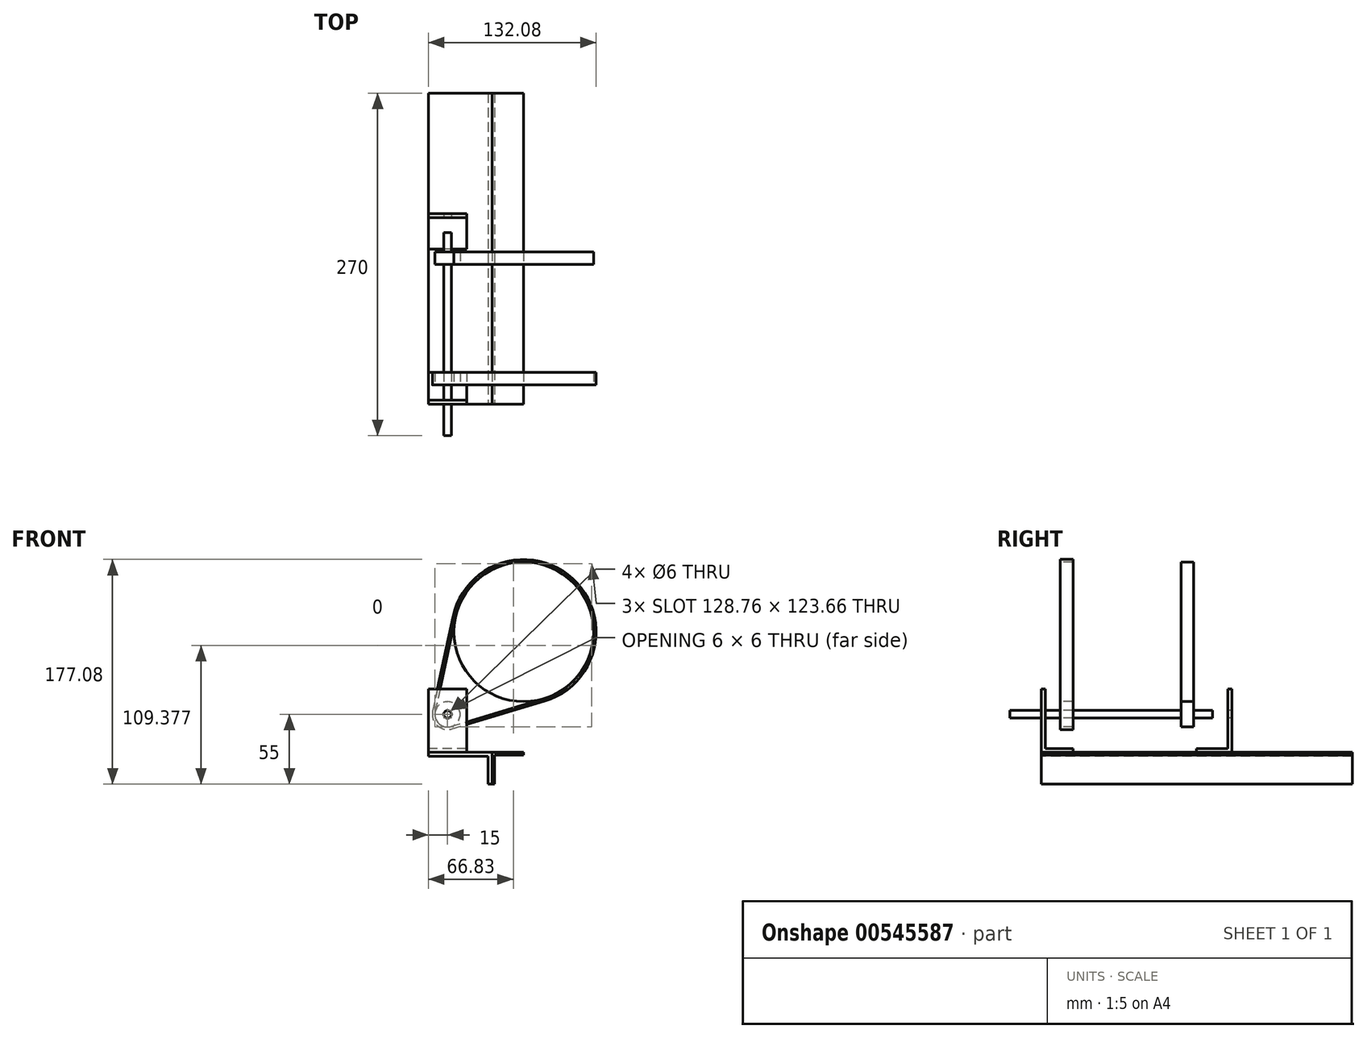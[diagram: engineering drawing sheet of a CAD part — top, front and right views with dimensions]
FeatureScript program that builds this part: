
annotation { "Feature Type Name" : "Feature", "Feature Type Description" : "" }
export const myFeature = defineFeature(function(context is Context, id is Id, definition is map)
    precondition{}
    {
        {
            var Q0;
            Q0=qCreatedBy(makeId("Front.planeOp"),FACE);
            cPlane(context, id + "F0", {"entities" : qUnion([Q0]), "cplaneType" : CPlaneType.OFFSET, "offset" : 15 * mm, "oppositeDirection" : true, "width" : 150 * mm, "height" : 150 * mm});
        }
        {
            var Q0;
            Q0=qCreatedBy(id+"F0.planeOp",FACE);
            cPlane(context, id + "F1", {"entities" : qUnion([Q0]), "cplaneType" : CPlaneType.OFFSET, "offset" : 95 * mm, "oppositeDirection" : true, "width" : 150 * mm, "height" : 150 * mm});
        }
        {
            var Q0;
            Q0=qCreatedBy(makeId("Front.planeOp"),FACE);
            var sketch = newSketch(context, id + "F2", { "sketchPlane" : qUnion([Q0])});
            skLineSegment(sketch, "E0", {"start": v(0, 0) * mm, "end": v(0, 25) * mm});
            skLineSegment(sketch, "E1", {"start": v(0, 25) * mm, "end": v(25, 25) * mm});
            skLineSegment(sketch, "E2", {"start": v(25, 25) * mm, "end": v(25, 23) * mm});
            skLineSegment(sketch, "E3", {"start": v(25, 23) * mm, "end": v(2, 23) * mm});
            skLineSegment(sketch, "E4", {"start": v(2, 23) * mm, "end": v(2, 0) * mm});
            skLineSegment(sketch, "E5", {"start": v(2, 0) * mm, "end": v(0, 0) * mm});
            skSolve(sketch);
        }
        {
            var Q0;
            Q0 = qSketchRegion(id + "F2", true);
            extrude(context, id + "F3", {"entities" : qUnion([Q0]), "oppositeDirection" : true, "depth" : 245 * mm, "offsetDistance" : 25 * mm});
        }
        {
            var Q0;
            Q0=qCreatedBy(makeId("Front.planeOp"),FACE);
            var sketch = newSketch(context, id + "F4", { "sketchPlane" : qUnion([Q0])});
            skLineSegment(sketch, "E6", {"start": v(0, 0) * mm, "end": v(0, 25) * mm});
            skLineSegment(sketch, "E7", {"start": v(0, 25) * mm, "end": v(-50, 25) * mm});
            skLineSegment(sketch, "E8", {"start": v(-50, 25) * mm, "end": v(-50, 22) * mm});
            skLineSegment(sketch, "E9", {"start": v(-50, 22) * mm, "end": v(-3, 22) * mm});
            skLineSegment(sketch, "E10", {"start": v(-3, 22) * mm, "end": v(-3, 0) * mm});
            skLineSegment(sketch, "E11", {"start": v(-3, 0) * mm, "end": v(0, 0) * mm});
            skSolve(sketch);
        }
        {
            var Q0;
            Q0 = qSketchRegion(id + "F4", true);
            extrude(context, id + "F5", {"entities" : qUnion([Q0]), "oppositeDirection" : true, "depth" : 245 * mm, "offsetDistance" : 25 * mm});
        }
        {
            var Q0;
            Q0=makeQuery(id+"F5.opExtrude","SWEPT_FACE",FACE,{"disambiguationData":[OSD([sQuery(id+"F4.wireOp",EDGE,"E8")])]});
            var sketch = newSketch(context, id + "F6", { "sketchPlane" : qUnion([Q0])});
            skLineSegment(sketch, "E12", {"start": v(0, 25) * mm, "end": v(-25, 25) * mm});
            skLineSegment(sketch, "E13", {"start": v(-25, 25) * mm, "end": v(-25, 28) * mm});
            skLineSegment(sketch, "E14", {"start": v(-25, 28) * mm, "end": v(-3, 28) * mm});
            skLineSegment(sketch, "E15", {"start": v(-3, 28) * mm, "end": v(-3, 75) * mm});
            skLineSegment(sketch, "E16", {"start": v(-3, 75) * mm, "end": v(0, 75) * mm});
            skLineSegment(sketch, "E17", {"start": v(0, 75) * mm, "end": v(0, 25) * mm});
            skLineSegment(sketch, "E18", {"start": v(0, 25) * mm, "end": v(-150, 25) * mm, "construction": true});
            skLineSegment(sketch, "E19", {"start": v(-150, 25) * mm, "end": v(-150, 75) * mm});
            skLineSegment(sketch, "E20", {"start": v(-150, 75) * mm, "end": v(-147, 75) * mm});
            skLineSegment(sketch, "E21", {"start": v(-147, 75) * mm, "end": v(-147, 28) * mm});
            skLineSegment(sketch, "E22", {"start": v(-147, 28) * mm, "end": v(-122, 28) * mm});
            skLineSegment(sketch, "E23", {"start": v(-122, 28) * mm, "end": v(-122, 25) * mm});
            skLineSegment(sketch, "E24", {"start": v(-122, 25) * mm, "end": v(-150, 25) * mm});
            skSolve(sketch);
        }
        {
            var Q0;
            Q0 = qSketchRegion(id + "F6", true);
            extrude(context, id + "F7", {"entities" : qUnion([Q0]), "oppositeDirection" : true, "depth" : 30 * mm, "offsetDistance" : 25 * mm});
        }
        {
            var Q0;
            Q0=makeQuery(id+"F7.opExtrude","SWEPT_FACE",FACE,{"disambiguationData":[OSD([sQuery(id+"F6.wireOp",EDGE,"E17")])]});
            var sketch = newSketch(context, id + "F8", { "sketchPlane" : qUnion([Q0])});
            skCircle(sketch, "E25", {"center": v(-35, 55) * mm, "radius": 3 * mm});
            skSolve(sketch);
        }
        {
            var Q0;
            Q0 = qSketchRegion(id + "F8", true);
            extrude(context, id + "F9", {"entities" : qUnion([Q0]), "operationType" : NewBodyOperationType.REMOVE, "endBound" : BoundingType.THROUGH_ALL, "oppositeDirection" : true, "depth" : 25 * mm, "offsetDistance" : 25 * mm});
        }
        {
            var Q0;
            Q0=qCreatedBy(makeId("Front.planeOp"),FACE);
            var sketch = newSketch(context, id + "F10", { "sketchPlane" : qUnion([Q0])});
            skCircle(sketch, "E26.0", {"center": v(-35, 55) * mm, "radius": 3 * mm});
            skSolve(sketch);
        }
        {
            var Q0;
            Q0 = qSketchRegion(id + "F10", true);
            extrude(context, id + "F11", {"entities" : qUnion([Q0]), "operationType" : NewBodyOperationType.ADD, "oppositeDirection" : true, "depth" : 135 * mm, "offsetDistance" : 25 * mm, "hasSecondDirection" : true, "secondDirectionOppositeDirection" : false, "secondDirectionDepth" : 25 * mm});
        }
        {
            var Q0;
            Q0=qCreatedBy(id+"F0.planeOp",FACE);
            var sketch = newSketch(context, id + "F12", { "sketchPlane" : qUnion([Q0])});
            skPoint(sketch, "E27.0", {"position": v(25, 25) * mm});
            skLineSegment(sketch, "E28", {"start": v(25, 25) * mm, "end": v(25, 120) * mm, "construction": true});
            skCircle(sketch, "E29", {"center": v(25, 120) * mm, "radius": 55 * mm});
            skCircle(sketch, "E30.0", {"center": v(-35, 55) * mm, "radius": 3 * mm});
            skCircle(sketch, "E31", {"center": v(-35, 55) * mm, "radius": 10 * mm});
            skSolve(sketch);
        }
        {
            var Q0;
            Q0 = qSketchRegion(id + "F12", true);
            extrude(context, id + "F13", {"entities" : qUnion([Q0]), "oppositeDirection" : true, "depth" : 10 * mm, "offsetDistance" : 25 * mm});
        }
        {
            var Q0;
            Q0=qCreatedBy(id+"F1.planeOp",FACE);
            var sketch = newSketch(context, id + "F14", { "sketchPlane" : qUnion([Q0])});
            skCircle(sketch, "E32.0.0", {"center": v(25, 120) * mm, "radius": 55 * mm});
            skCircle(sketch, "E33.0", {"center": v(-35, 55) * mm, "radius": 10 * mm});
            skSolve(sketch);
        }
        {
            var Q0;
            Q0 = qSketchRegion(id + "F14", true);
            extrude(context, id + "F15", {"entities" : qUnion([Q0]), "oppositeDirection" : true, "depth" : 10 * mm, "offsetDistance" : 25 * mm});
        }
        {
            var Q0;
            Q0=qCreatedBy(id+"F0.planeOp",FACE);
            var sketch = newSketch(context, id + "F16", { "sketchPlane" : qUnion([Q0])});
            skLineSegment(sketch, "E34", {"start": v(-32.13, 45.41) * mm, "end": v(40.8, 67.24) * mm});
            skLineSegment(sketch, "E35", {"start": v(-28.86, 131.53) * mm, "end": v(-44.79, 57.1) * mm});
            skArc(sketch, "E36", {"start": v(40.8, 67.24) * mm, "mid": v(62.36, 160.47) * mm, "end": v(-28.86, 131.53) * mm});
            skArc(sketch, "E37", {"start": v(-44.79, 57.1) * mm, "mid": v(-41.79, 47.64) * mm, "end": v(-32.13, 45.41) * mm});
            skArc(sketch, "E38.0", {"start": v(41.37, 65.32) * mm, "mid": v(63.71, 161.94) * mm, "end": v(-30.81, 131.95) * mm});
            skLineSegment(sketch, "E38.1", {"start": v(-31.56, 43.5) * mm, "end": v(41.37, 65.32) * mm});
            skArc(sketch, "E38.2", {"start": v(-46.74, 57.51) * mm, "mid": v(-43.15, 46.18) * mm, "end": v(-31.56, 43.5) * mm});
            skLineSegment(sketch, "E38.3", {"start": v(-30.81, 131.95) * mm, "end": v(-46.74, 57.51) * mm});
            skSolve(sketch);
        }
        {
            var Q0;
            Q0 = qSketchRegion(id + "F16", true);
            extrude(context, id + "F17", {"entities" : qUnion([Q0]), "oppositeDirection" : true, "depth" : 10 * mm, "offsetDistance" : 25 * mm});
        }
    });
